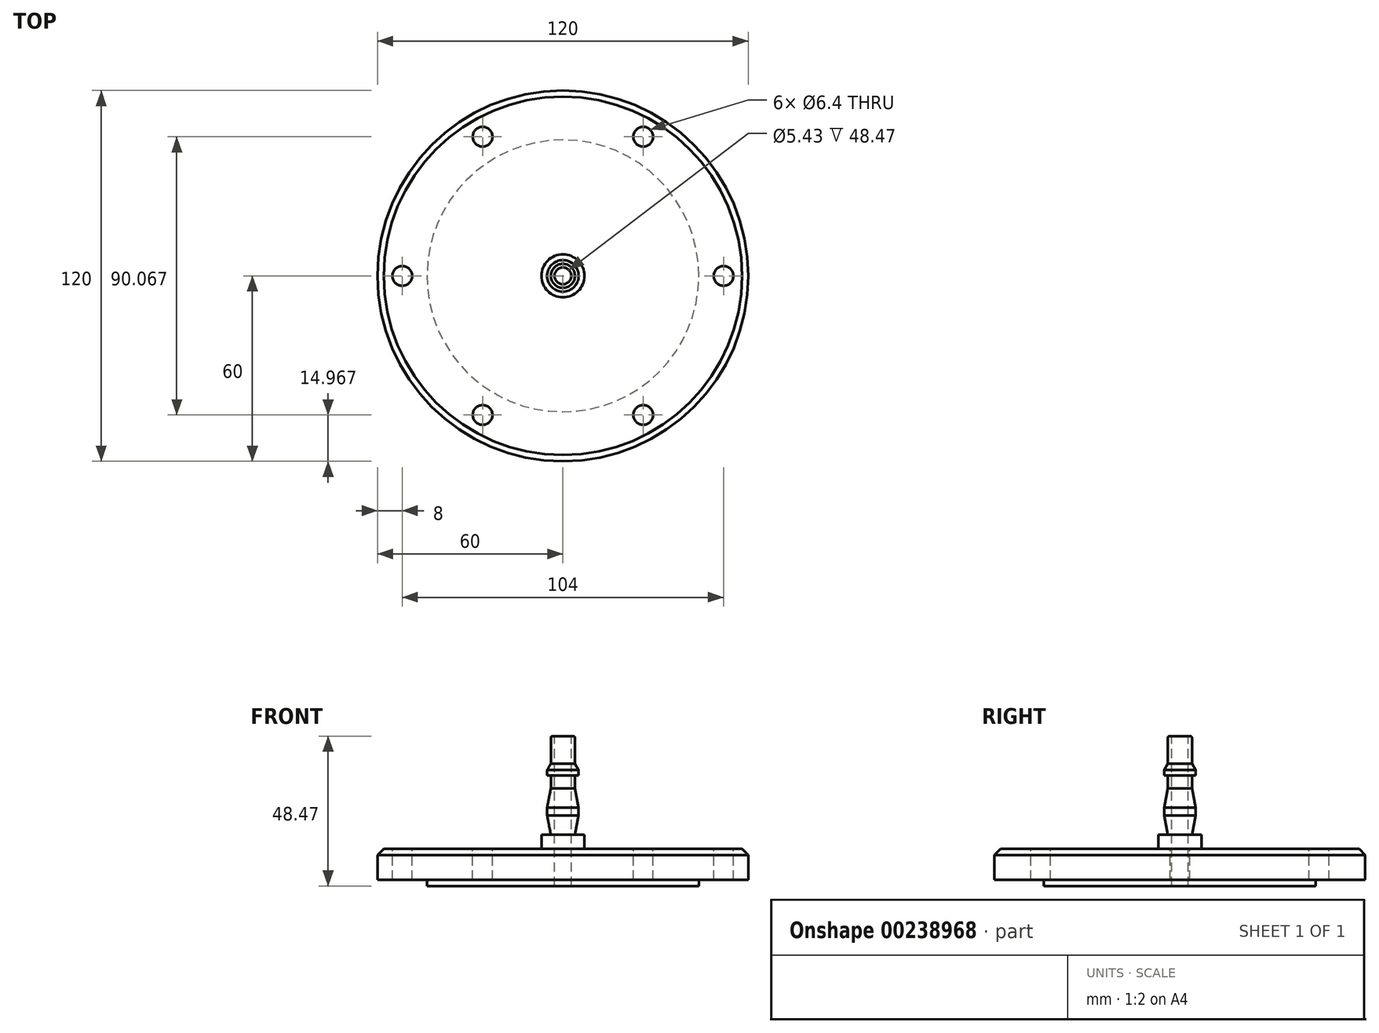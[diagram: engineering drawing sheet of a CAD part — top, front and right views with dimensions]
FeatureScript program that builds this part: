
annotation { "Feature Type Name" : "Feature", "Feature Type Description" : "" }
export const myFeature = defineFeature(function(context is Context, id is Id, definition is map)
    precondition{}
    {
        {
            var Q0;
            Q0=qCreatedBy(makeId("Front.planeOp"),FACE);
            var sketch = newSketch(context, id + "F0", { "sketchPlane" : qUnion([Q0])});
            skPoint(sketch, "E0", {"position": v(-49.47, 3.56) * mm});
            skLineSegment(sketch, "E1.trimOffspring", {"start": v(-44, -2) * mm, "end": v(-44, 0) * mm});
            skLineSegment(sketch, "E2", {"start": v(-60, 10) * mm, "end": v(-60, 0) * mm});
            skLineSegment(sketch, "E3", {"start": v(-60, 10) * mm, "end": v(-2.72, 10) * mm});
            skLineSegment(sketch, "E4", {"start": v(-44, -2) * mm, "end": v(-2.72, -2) * mm});
            skLineSegment(sketch, "E5", {"start": v(-60, 0) * mm, "end": v(-44, 0) * mm});
            skLineSegment(sketch, "E6", {"start": v(-2.72, 10) * mm, "end": v(-2.71, -2) * mm});
            skLineSegment(sketch, "E7", {"start": v(0, 26.74) * mm, "end": v(0, -21.81) * mm, "construction": true});
            skSolve(sketch);
        }
        {
            var Q0;
            Q0=makeQuery(id+"F0.imprint","IMPRINT",FACE,{"disambiguationData":[TD([[makeQuery(id+"F0.imprint","IMPRINT",EDGE,{"derivedFrom":sQuery(id+"F0.wireOp",EDGE,"E1.trimOffspring")}),-1.0]])]});
            var Q1;
            Q1=sQuery(id+"F0.wireOp",EDGE,"E7");
            revolve(context, id + "F1", {"entities" : qUnion([Q0]), "axis" : qUnion([Q1]), "revolveType" : RevolveType.FULL});
        }
        {
            var Q0;
            Q0=makeQuery(id+"F1.opRevolve","SWEPT_FACE",FACE,{"disambiguationData":[OSD([sQuery(id+"F0.wireOp",EDGE,"E3")])]});
            cPlane(context, id + "F2", {"entities" : qUnion([Q0]), "cplaneType" : CPlaneType.OFFSET, "offset" : 0 * mm, "width" : 150 * mm, "height" : 150 * mm});
        }
        {
            var Q0;
            Q0=qCreatedBy(id+"F2.planeOp",FACE);
            var sketch = newSketch(context, id + "F3", { "sketchPlane" : qUnion([Q0])});
            skCircle(sketch, "E8", {"center": v(0, 0) * mm, "radius": 52 * mm, "construction": true});
            skLineSegment(sketch, "E9", {"start": v(0, 0) * mm, "end": v(-47.93, 83) * mm, "construction": true});
            skPoint(sketch, "E10", {"position": v(-26, 45.03) * mm});
            skPoint(sketch, "E11.1.0", {"position": v(-52, 0) * mm});
            skPoint(sketch, "E11.2.0", {"position": v(-26, -45.03) * mm});
            skPoint(sketch, "E11.3.0", {"position": v(26, -45.03) * mm});
            skPoint(sketch, "E11.4.0", {"position": v(52, 0) * mm});
            skPoint(sketch, "E11.5.0", {"position": v(26, 45.03) * mm});
            skSolve(sketch);
        }
        {
            var Q0;
            Q0=sQuery(id+"F3.wireOp",VERTEX,"E10");
            var Q1;
            Q1=sQuery(id+"F3.wireOp",VERTEX,"E11.1.0");
            var Q2;
            Q2=sQuery(id+"F3.wireOp",VERTEX,"E11.2.0");
            var Q3;
            Q3=sQuery(id+"F3.wireOp",VERTEX,"E11.3.0");
            var Q4;
            Q4=sQuery(id+"F3.wireOp",VERTEX,"E11.4.0");
            var Q5;
            Q5=sQuery(id+"F3.wireOp",VERTEX,"E11.5.0");
            var Q6;
            Q6=makeQuery(id+"F1.opRevolve","SWEPT_BODY",BODY,{"disambiguationData":[OSD([sQuery(id+"F0.wireOp",EDGE,"3d11c7ee-7c3a-4b72-8a72-74c4a18ef5c6"),sQuery(id+"F0.wireOp",EDGE,"E1.trimOffspring"),sQuery(id+"F0.wireOp",EDGE,"E2"),sQuery(id+"F0.wireOp",EDGE,"E3"),sQuery(id+"F0.wireOp",EDGE,"E4"),sQuery(id+"F0.wireOp",EDGE,"E5")])]});
            hole(context, id + "F4", {"style" : HoleStyle.SIMPLE, "endStyle" : HoleEndStyle.THROUGH, "holeDiameter" : 6.4 * mm, "locations" : qUnion([Q0, Q1, Q2, Q3, Q4, Q5]), "scope" : qUnion([Q6]), "isTappedThrough" : true});
        }
        {
            var Q0;
            Q0=makeQuery(id+"F1.opRevolve","SWEPT_EDGE",EDGE,{"disambiguationData":[OSD([sQuery(id+"F0.wireOp",EDGE,"E2"),sQuery(id+"F0.wireOp",EDGE,"E3")])]});
            chamfer(context, id + "F5", {"entities" : qUnion([Q0]), "width" : 2 * mm, "tangentPropagation" : true});
        }
        {
            var Q0;
            Q0=qCreatedBy(makeId("Front.planeOp"),FACE);
            var sketch = newSketch(context, id + "F6", { "sketchPlane" : qUnion([Q0])});
            skLineSegment(sketch, "E12.0", {"start": v(-3.91, 37.61) * mm, "end": v(-3.91, 45.97) * mm});
            skArc(sketch, "E13.0", {"start": v(-3.91, 45.97) * mm, "mid": v(-3.76, 46.32) * mm, "end": v(-3.41, 46.47) * mm});
            skLineSegment(sketch, "E13.1", {"start": v(-3.41, 46.47) * mm, "end": v(-2.72, 46.47) * mm});
            skLineSegment(sketch, "E14.0", {"start": v(-5.09, 35.51) * mm, "end": v(-3.91, 37.61) * mm});
            skLineSegment(sketch, "E15.1", {"start": v(-5.09, 33.81) * mm, "end": v(-5.09, 35.51) * mm});
            skLineSegment(sketch, "E15.3", {"start": v(-3.91, 29.6) * mm, "end": v(-3.91, 33.81) * mm});
            skLineSegment(sketch, "E15.4", {"start": v(-5.1, 23.4) * mm, "end": v(-3.91, 29.6) * mm});
            skLineSegment(sketch, "E15.5", {"start": v(-3.91, 14.6) * mm, "end": v(-5.1, 20.8) * mm});
            skLineSegment(sketch, "E15.6", {"start": v(-3.48, 14.6) * mm, "end": v(-6.95, 14.6) * mm});
            skFitSpline(sketch, "E16.0", {"points": [v(-3.48, 14.6) * mm, v(-3.62, 14.6) * mm, v(-3.9, 14.6) * mm, v(-4.34, 14.56) * mm, v(-4.71, 14.52) * mm, v(-4.97, 14.48) * mm, v(-5.12, 14.45) * mm, v(-5.24, 14.43) * mm, v(-5.33, 14.41) * mm, v(-5.47, 14.39) * mm, v(-5.71, 14.33) * mm, v(-6.07, 14.25) * mm, v(-6.5, 14.12) * mm, v(-6.8, 14.03) * mm, v(-6.95, 13.98) * mm], "construction": true});
            skLineSegment(sketch, "E16.1", {"start": v(-6.95, 14.6) * mm, "end": v(-6.95, 10) * mm});
            skLineSegment(sketch, "E17.0", {"start": v(-2.72, 10) * mm, "end": v(-2.72, 46.47) * mm});
            skLineSegment(sketch, "E18", {"start": v(0, -2.13) * mm, "end": v(0, 50.87) * mm, "construction": true});
            skLineSegment(sketch, "E19.trimOffspring", {"start": v(-3.91, 33.81) * mm, "end": v(-5.09, 33.81) * mm});
            skLineSegment(sketch, "E20", {"start": v(-5.1, 20.8) * mm, "end": v(-5.1, 23.4) * mm});
            skPoint(sketch, "E21", {"position": v(0, 10) * mm});
            skLineSegment(sketch, "E22", {"start": v(-6.95, 10) * mm, "end": v(-2.72, 10) * mm});
            skSolve(sketch);
        }
        {
            var Q0;
            Q0 = qSketchRegion(id + "F6", true);
            var Q1;
            Q1=sQuery(id+"F6.wireOp",EDGE,"E18");
            revolve(context, id + "F7", {"operationType" : NewBodyOperationType.ADD, "entities" : qUnion([Q0]), "axis" : qUnion([Q1]), "revolveType" : RevolveType.FULL});
        }
    });
